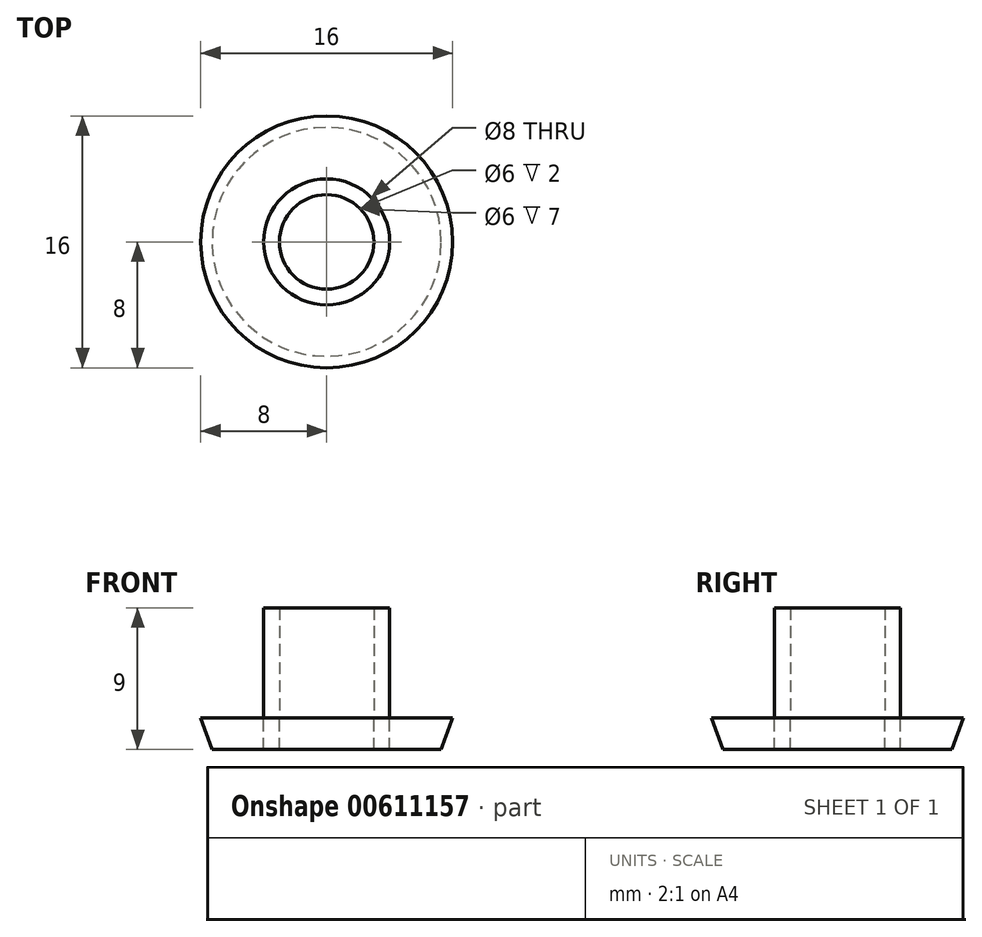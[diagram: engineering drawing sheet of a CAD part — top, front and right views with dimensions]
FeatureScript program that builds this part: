
annotation { "Feature Type Name" : "Feature", "Feature Type Description" : "" }
export const myFeature = defineFeature(function(context is Context, id is Id, definition is map)
    precondition{}
    {
        {
            var Q0;
            Q0=qCreatedBy(makeId("Top.planeOp"),FACE);
            var sketch = newSketch(context, id + "F0", { "sketchPlane" : qUnion([Q0])});
            skCircle(sketch, "E0", {"center": v(0, 0) * mm, "radius": 4 * mm});
            skCircle(sketch, "E1", {"center": v(0, 0) * mm, "radius": 8 * mm});
            skCircle(sketch, "E2.0", {"center": v(0, 0) * mm, "radius": 3 * mm});
            skSolve(sketch);
        }
        {
            var Q0;
            Q0=makeQuery(id+"F0.imprint","IMPRINT",FACE,{"disambiguationData":[TD([[makeQuery(id+"F0.imprint","IMPRINT",EDGE,{"derivedFrom":sQuery(id+"F0.wireOp",EDGE,"E0")}),1.0]])]});
            extrude(context, id + "F1", {"entities" : qUnion([Q0]), "depth" : 7 * mm, "offsetDistance" : 25 * mm});
        }
        {
            var Q0;
            Q0 = qSketchRegion(id + "F0", true);
            extrude(context, id + "F2", {"entities" : qUnion([Q0]), "oppositeDirection" : true, "depth" : 2 * mm, "offsetDistance" : 25 * mm});
        }
        {
            var Q0;
            Q0=makeQuery(id+"F2.opExtrude","CAP_EDGE",EDGE,{"disambiguationData":[OSD([sQuery(id+"F0.wireOp",EDGE,"E1")])],"isStart":false});
            chamfer(context, id + "F3", {"entities" : qUnion([Q0]), "chamferType" : ChamferType.OFFSET_ANGLE, "width" : 2 * mm, "oppositeDirection" : false, "angle" : 20 * degree, "tangentPropagation" : true});
        }
        {
            var Q0;
            Q0=makeQuery(id+"F1.opExtrude","CAP_FACE",FACE,{"disambiguationData":[OSD([sQuery(id+"F0.wireOp",EDGE,"E0"),sQuery(id+"F0.wireOp",EDGE,"E2.0")])],"isStart":true});
            extrude(context, id + "F4", {"entities" : qUnion([Q0]), "depth" : 2 * mm, "offsetDistance" : 25 * mm});
        }
    });
